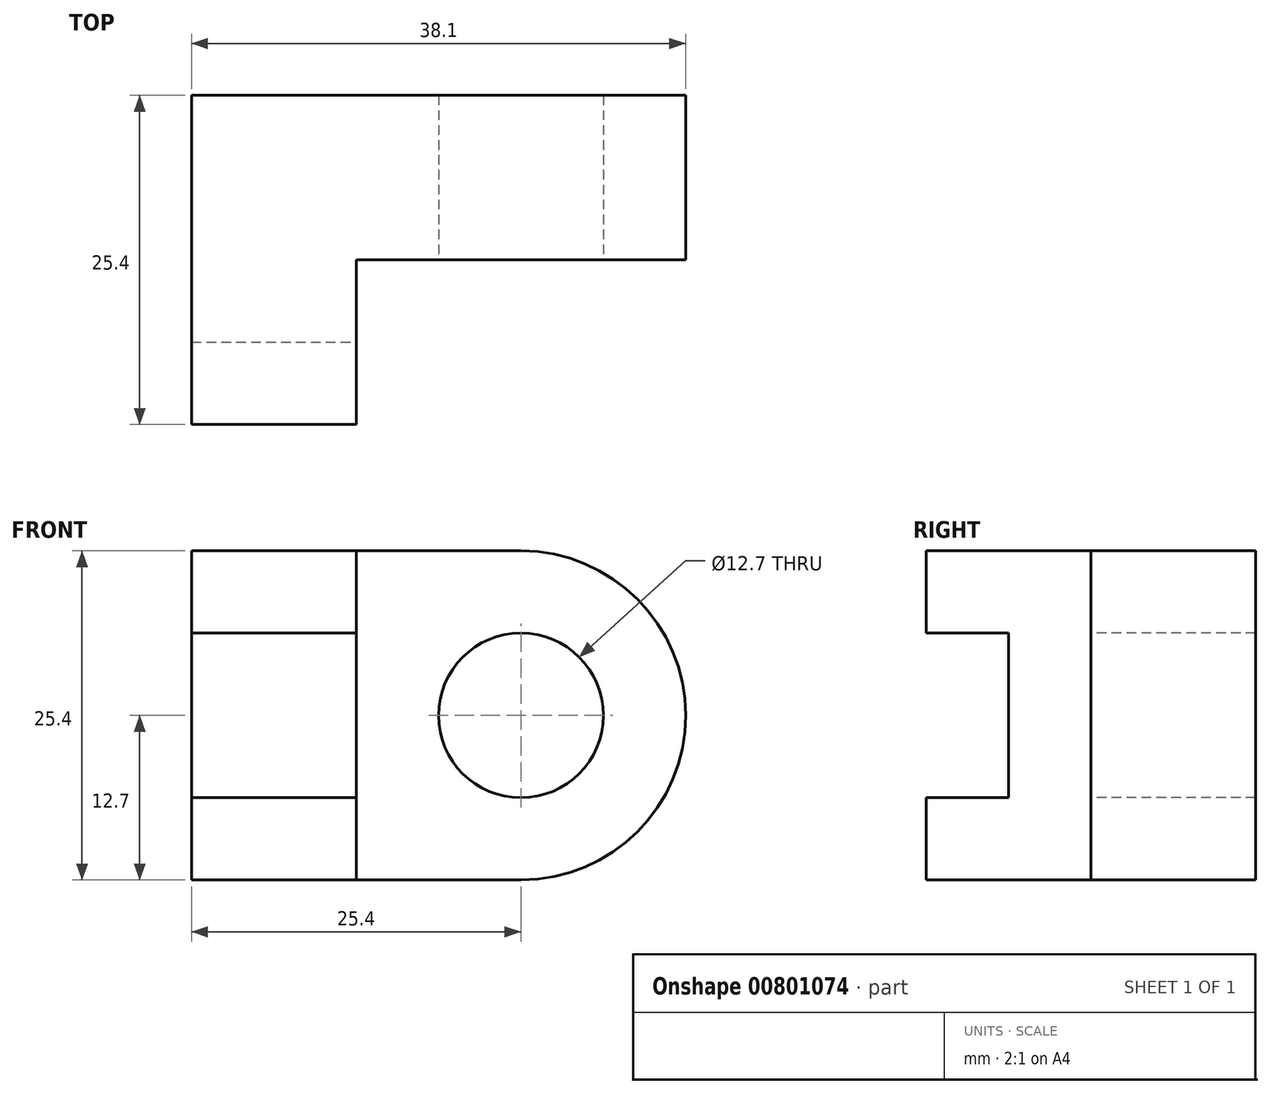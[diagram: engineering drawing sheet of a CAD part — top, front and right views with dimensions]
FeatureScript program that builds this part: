
annotation { "Feature Type Name" : "Feature", "Feature Type Description" : "" }
export const myFeature = defineFeature(function(context is Context, id is Id, definition is map)
    precondition{}
    {
        {
            var Q0;
            Q0=qCreatedBy(makeId("Front.planeOp"),FACE);
            var sketch = newSketch(context, id + "F0", { "sketchPlane" : qUnion([Q0])});
            skLineSegment(sketch, "E0", {"start": v(0, 0) * mm, "end": v(38.1, 0) * mm});
            skLineSegment(sketch, "E1", {"start": v(0, 0) * mm, "end": v(0, 25.4) * mm});
            skLineSegment(sketch, "E2", {"start": v(0, 25.4) * mm, "end": v(38.1, 25.4) * mm});
            skLineSegment(sketch, "E3", {"start": v(38.1, 0) * mm, "end": v(38.1, 25.4) * mm});
            skSolve(sketch);
        }
        {
            var Q0;
            Q0=makeQuery(id+"F0.imprint","IMPRINT",FACE,{"disambiguationData":[TD([[makeQuery(id+"F0.imprint","IMPRINT",EDGE,{"derivedFrom":sQuery(id+"F0.wireOp",EDGE,"E0")}),1.0]])]});
            extrude(context, id + "F1", {"entities" : qUnion([Q0]), "depth" : 25.4 * mm, "offsetDistance" : 25.4 * mm});
        }
        {
            var Q0;
            Q0=makeQuery(id+"F1.opExtrude","CAP_FACE",FACE,{"disambiguationData":[OSD([sQuery(id+"F0.wireOp",EDGE,"E0"),sQuery(id+"F0.wireOp",EDGE,"E1"),sQuery(id+"F0.wireOp",EDGE,"E2"),sQuery(id+"F0.wireOp",EDGE,"E3")])],"isStart":false});
            var sketch = newSketch(context, id + "F2", { "sketchPlane" : qUnion([Q0])});
            skLineSegment(sketch, "E4", {"start": v(0, 25.4) * mm, "end": v(12.7, 25.4) * mm, "construction": true});
            skLineSegment(sketch, "E5", {"start": v(12.7, 25.4) * mm, "end": v(12.7, 0) * mm});
            skSolve(sketch);
        }
        {
            var Q0;
            Q0 = qSketchRegion(id + "F2", true);
            var Q1;
            {var subQ0=sQuery(id+"F2.wireOp",EDGE,"E5");Q1=makeQuery(id+"F2.imprint","IMPRINT",FACE,{"disambiguationData":[TD([[makeQuery(id+"F2.imprint","IMPRINT",EDGE,{"derivedFrom":subQ0}),1.0]])]});}
            extrude(context, id + "F3", {"entities" : qUnion([Q0, Q1]), "operationType" : NewBodyOperationType.REMOVE, "oppositeDirection" : true, "depth" : 12.7 * mm, "offsetDistance" : 25.4 * mm});
        }
        {
            var Q0;
            Q0=makeQuery(id+"F3.boolean.opBoolean","COPY",FACE,{"derivedFrom":makeQuery(id+"F3.opExtrude","CAP_FACE",FACE,{"disambiguationData":[OSD([sQuery(id+"F0.wireOp",EDGE,"E0"),sQuery(id+"F0.wireOp",EDGE,"E2"),sQuery(id+"F0.wireOp",EDGE,"E3"),sQuery(id+"F2.wireOp",EDGE,"E5")])],"isStart":false})});
            var sketch = newSketch(context, id + "F4", { "sketchPlane" : qUnion([Q0])});
            skArc(sketch, "E6", {"start": v(25.4, 0) * mm, "mid": v(38.1, 12.7) * mm, "end": v(25.4, 25.4) * mm});
            skCircle(sketch, "E7", {"center": v(25.4, 12.7) * mm, "radius": 6.35 * mm});
            skSolve(sketch);
        }
        {
            var Q0;
            Q0 = qSketchRegion(id + "F4", true);
            var Q1;
            {var subQ0=sQuery(id+"F4.wireOp",EDGE,"E6");var subQ1=makeQuery(id+"F3.boolean.opBoolean","COPY",EDGE,{"derivedFrom":makeQuery(id+"F3.opExtrude","CAP_EDGE",EDGE,{"disambiguationData":[OSD([sQuery(id+"F0.wireOp",EDGE,"E0")])],"isStart":false})});var subQ2=makeQuery(id+"F4.imprint","INTERSECT",VERTEX,{"derivedFrom":[subQ1,subQ0]});Q1=makeQuery(id+"F4.imprint","IMPRINT",FACE,{"disambiguationData":[TD([[makeQuery(id+"F4.imprint","IMPRINT",EDGE,{"disambiguationData":[TD([[subQ2,-1.0]])],"derivedFrom":subQ0}),-1.0]])]});}
            var Q2;
            {var subQ0=sQuery(id+"F4.wireOp",EDGE,"E6");var subQ1=makeQuery(id+"F3.boolean.opBoolean","COPY",EDGE,{"derivedFrom":makeQuery(id+"F3.opExtrude","CAP_EDGE",EDGE,{"disambiguationData":[OSD([sQuery(id+"F0.wireOp",EDGE,"E2")])],"isStart":false})});var subQ2=makeQuery(id+"F4.imprint","INTERSECT",VERTEX,{"derivedFrom":[subQ1,subQ0]});Q2=makeQuery(id+"F4.imprint","IMPRINT",FACE,{"disambiguationData":[TD([[makeQuery(id+"F4.imprint","IMPRINT",EDGE,{"disambiguationData":[TD([[subQ2,1.0]])],"derivedFrom":subQ0}),-1.0]])]});}
            extrude(context, id + "F5", {"entities" : qUnion([Q0, Q1, Q2]), "operationType" : NewBodyOperationType.REMOVE, "endBound" : BoundingType.UP_TO_NEXT, "oppositeDirection" : true, "depth" : 25.4 * mm, "offsetDistance" : 25.4 * mm});
        }
        {
            var Q0;
            Q0=makeQuery(id+"F3.boolean.opBoolean","COPY",FACE,{"derivedFrom":makeQuery(id+"F3.opExtrude","SWEPT_FACE",FACE,{"disambiguationData":[OSD([sQuery(id+"F2.wireOp",EDGE,"E5")])]})});
            var sketch = newSketch(context, id + "F6", { "sketchPlane" : qUnion([Q0])});
            skLineSegment(sketch, "E8", {"start": v(-25.4, 25.4) * mm, "end": v(-25.4, 19.05) * mm, "construction": true});
            skLineSegment(sketch, "E9", {"start": v(-25.4, 19.05) * mm, "end": v(-19.05, 19.05) * mm});
            skLineSegment(sketch, "E10", {"start": v(-19.05, 19.05) * mm, "end": v(-19.05, 6.35) * mm});
            skLineSegment(sketch, "E11", {"start": v(-19.05, 6.35) * mm, "end": v(-25.4, 6.35) * mm});
            skSolve(sketch);
        }
        {
            var Q0;
            {var subQ0=sQuery(id+"F6.wireOp",EDGE,"E9");Q0=makeQuery(id+"F6.imprint","IMPRINT",FACE,{"disambiguationData":[TD([[makeQuery(id+"F6.imprint","IMPRINT",EDGE,{"derivedFrom":subQ0}),-1.0]])]});}
            extrude(context, id + "F7", {"entities" : qUnion([Q0]), "operationType" : NewBodyOperationType.REMOVE, "oppositeDirection" : true, "depth" : 25.4 * mm, "offsetDistance" : 25.4 * mm});
        }
    });
